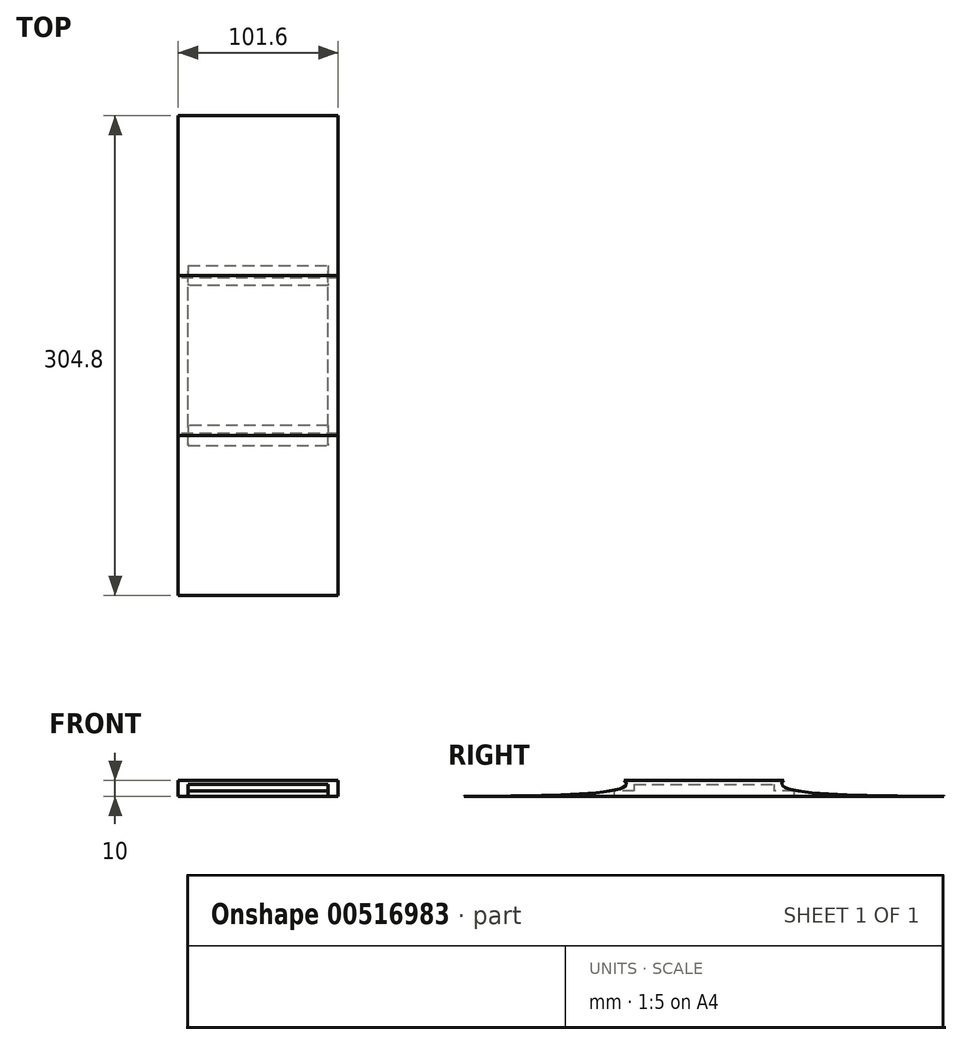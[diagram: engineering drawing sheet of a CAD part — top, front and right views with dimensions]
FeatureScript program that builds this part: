
annotation { "Feature Type Name" : "Feature", "Feature Type Description" : "" }
export const myFeature = defineFeature(function(context is Context, id is Id, definition is map)
    precondition{}
    {
        {
            var Q0;
            Q0=qCreatedBy(makeId("Top.planeOp"),FACE);
            var sketch = newSketch(context, id + "F0", { "sketchPlane" : qUnion([Q0])});
            skLineSegment(sketch, "E0.bottom", {"start": v(-50.8, 50.8) * mm, "end": v(50.8, 50.8) * mm});
            skLineSegment(sketch, "E0.top", {"start": v(-50.8, -50.8) * mm, "end": v(50.8, -50.8) * mm});
            skLineSegment(sketch, "E0.left", {"start": v(-50.8, 50.8) * mm, "end": v(-50.8, -50.8) * mm});
            skLineSegment(sketch, "E0.right", {"start": v(50.8, 50.8) * mm, "end": v(50.8, -50.8) * mm});
            skPoint(sketch, "E0.middle", {"position": v(0, 0) * mm});
            skLineSegment(sketch, "E1.top", {"start": v(-50.8, 152.4) * mm, "end": v(50.8, 152.4) * mm});
            skLineSegment(sketch, "E1.left", {"start": v(-50.8, 50.8) * mm, "end": v(-50.8, 152.4) * mm});
            skLineSegment(sketch, "E1.right", {"start": v(50.8, 50.8) * mm, "end": v(50.8, 152.4) * mm});
            skLineSegment(sketch, "E2.left", {"start": v(-50.8, -50.8) * mm, "end": v(-50.8, 50.8) * mm});
            skLineSegment(sketch, "E3.top", {"start": v(-50.8, -152.4) * mm, "end": v(50.8, -152.4) * mm});
            skLineSegment(sketch, "E3.left", {"start": v(-50.8, -50.8) * mm, "end": v(-50.8, -152.4) * mm});
            skLineSegment(sketch, "E3.right", {"start": v(50.8, -50.8) * mm, "end": v(50.8, -152.4) * mm});
            skSolve(sketch);
        }
        {
            var Q0;
            Q0 = qSketchRegion(id + "F0", true);
            extrude(context, id + "F1", {"entities" : qUnion([Q0]), "depth" : 10 * mm, "offsetDistance" : 25 * mm});
        }
        {
            var Q0;
            Q0=makeQuery(id+"F1.opExtrude","CAP_FACE",FACE,{"disambiguationData":[OSD([sQuery(id+"F0.wireOp",EDGE,"E1.top"),sQuery(id+"F0.wireOp",EDGE,"E1.left"),sQuery(id+"F0.wireOp",EDGE,"E1.right"),sQuery(id+"F0.wireOp",EDGE,"E2.bottom"),sQuery(id+"F0.wireOp",EDGE,"E2.top"),sQuery(id+"F0.wireOp",EDGE,"E2.right"),sQuery(id+"F0.wireOp",EDGE,"E3.top"),sQuery(id+"F0.wireOp",EDGE,"E3.left"),sQuery(id+"F0.wireOp",EDGE,"E3.right"),sQuery(id+"F0.wireOp",EDGE,"qjwUIyOi-5xXZ-Iw75-sEBW-qZ2opq0OJGhn.bottom"),sQuery(id+"F0.wireOp",EDGE,"qjwUIyOi-5xXZ-Iw75-sEBW-qZ2opq0OJGhn.top"),sQuery(id+"F0.wireOp",EDGE,"qjwUIyOi-5xXZ-Iw75-sEBW-qZ2opq0OJGhn.right")])],"isStart":true});
            var sketch = newSketch(context, id + "F2", { "sketchPlane" : qUnion([Q0])});
            skLineSegment(sketch, "E4.bottom", {"start": v(-44.45, 44.45) * mm, "end": v(44.45, 44.45) * mm});
            skLineSegment(sketch, "E4.top", {"start": v(-44.45, -44.45) * mm, "end": v(44.45, -44.45) * mm});
            skLineSegment(sketch, "E4.left", {"start": v(-44.45, 44.45) * mm, "end": v(-44.45, -44.45) * mm});
            skLineSegment(sketch, "E4.right", {"start": v(44.45, 44.45) * mm, "end": v(44.45, -44.45) * mm});
            skPoint(sketch, "E4.middle", {"position": v(0, 0) * mm});
            skSolve(sketch);
        }
        {
            var Q0;
            Q0 = qSketchRegion(id + "F2", true);
            extrude(context, id + "F3", {"entities" : qUnion([Q0]), "operationType" : NewBodyOperationType.REMOVE, "oppositeDirection" : true, "depth" : 7.5 * mm, "offsetDistance" : 25 * mm});
        }
        {
            var Q0;
            Q0=makeQuery(id+"F1.opExtrude","CAP_FACE",FACE,{"disambiguationData":[OSD([sQuery(id+"F0.wireOp",EDGE,"E1.top"),sQuery(id+"F0.wireOp",EDGE,"E1.left"),sQuery(id+"F0.wireOp",EDGE,"E1.right"),sQuery(id+"F0.wireOp",EDGE,"E2.bottom"),sQuery(id+"F0.wireOp",EDGE,"E2.top"),sQuery(id+"F0.wireOp",EDGE,"E2.right"),sQuery(id+"F0.wireOp",EDGE,"E3.top"),sQuery(id+"F0.wireOp",EDGE,"E3.left"),sQuery(id+"F0.wireOp",EDGE,"E3.right"),sQuery(id+"F0.wireOp",EDGE,"qjwUIyOi-5xXZ-Iw75-sEBW-qZ2opq0OJGhn.bottom"),sQuery(id+"F0.wireOp",EDGE,"qjwUIyOi-5xXZ-Iw75-sEBW-qZ2opq0OJGhn.top"),sQuery(id+"F0.wireOp",EDGE,"qjwUIyOi-5xXZ-Iw75-sEBW-qZ2opq0OJGhn.right")])],"isStart":true});
            var sketch = newSketch(context, id + "F4", { "sketchPlane" : qUnion([Q0])});
            skLineSegment(sketch, "E5.left", {"start": v(-44.45, 44.45) * mm, "end": v(-44.45, -44.45) * mm});
            skLineSegment(sketch, "E6.bottom", {"start": v(-44.45, 44.45) * mm, "end": v(44.45, 44.45) * mm});
            skLineSegment(sketch, "E6.top", {"start": v(-44.45, 57.15) * mm, "end": v(44.45, 57.15) * mm});
            skLineSegment(sketch, "E6.left", {"start": v(-44.45, 44.45) * mm, "end": v(-44.45, 57.15) * mm});
            skLineSegment(sketch, "E6.right", {"start": v(44.45, 44.45) * mm, "end": v(44.45, 57.15) * mm});
            skLineSegment(sketch, "E7.left", {"start": v(44.45, 44.45) * mm, "end": v(44.45, -44.45) * mm});
            skLineSegment(sketch, "E8.bottom", {"start": v(-44.45, -44.45) * mm, "end": v(44.45, -44.45) * mm});
            skLineSegment(sketch, "E8.top", {"start": v(-44.45, -57.15) * mm, "end": v(44.45, -57.15) * mm});
            skLineSegment(sketch, "E8.left", {"start": v(-44.45, -44.45) * mm, "end": v(-44.45, -57.15) * mm});
            skLineSegment(sketch, "E8.right", {"start": v(44.45, -44.45) * mm, "end": v(44.45, -57.15) * mm});
            skSolve(sketch);
        }
        {
            var Q0;
            Q0 = qSketchRegion(id + "F4", true);
            extrude(context, id + "F5", {"entities" : qUnion([Q0]), "operationType" : NewBodyOperationType.REMOVE, "oppositeDirection" : true, "depth" : 3.33 * mm, "offsetDistance" : 25.4 * mm});
        }
        {
            var Q0;
            Q0=makeQuery(id+"F1.opExtrude","SWEPT_FACE",FACE,{"disambiguationData":[OSD([sQuery(id+"F0.wireOp",EDGE,"E1.left"),sQuery(id+"F0.wireOp",EDGE,"E2.left"),sQuery(id+"F0.wireOp",EDGE,"E3.left")])]});
            var sketch = newSketch(context, id + "F6", { "sketchPlane" : qUnion([Q0])});
            skPoint(sketch, "E9", {"position": v(-50.8, 0) * mm});
            skPoint(sketch, "E10", {"position": v(50.8, 0) * mm});
            skFitSpline(sketch, "E11", {"points": [v(-152.4, 0) * mm, v(-50.8, 10) * mm], "startDerivative": vector(119.67, 0) * mm, "endDerivative": vector(-38.48, 30) * mm});
            skPoint(sketch, "E12", {"position": v(-152.4, 10) * mm});
            skFitSpline(sketch, "E13.MirrorCS", {"points": [v(152.4, 0) * mm, v(50.8, 10) * mm], "startDerivative": vector(-119.67, 0) * mm, "endDerivative": vector(38.48, 30) * mm});
            skPoint(sketch, "E14.MirrorP", {"position": v(152.4, 10) * mm});
            skSolve(sketch);
        }
        {
            var Q0;
            Q0 = qSketchRegion(id + "F6", true);
            var Q1;
            {var subQ0=sQuery(id+"F6.wireOp",EDGE,"E11");Q1=makeQuery(id+"F6.imprint","IMPRINT",FACE,{"disambiguationData":[TD([[makeQuery(id+"F6.imprint","IMPRINT",EDGE,{"derivedFrom":subQ0}),1.0]])]});}
            var Q2;
            {var subQ0=sQuery(id+"F6.wireOp",EDGE,"E13.MirrorCS");Q2=makeQuery(id+"F6.imprint","IMPRINT",FACE,{"disambiguationData":[TD([[makeQuery(id+"F6.imprint","IMPRINT",EDGE,{"derivedFrom":subQ0}),-1.0]])]});}
            extrude(context, id + "F7", {"entities" : qUnion([Q0, Q1, Q2]), "operationType" : NewBodyOperationType.REMOVE, "oppositeDirection" : true, "depth" : 103.63 * mm, "offsetDistance" : 25.4 * mm});
        }
    });
